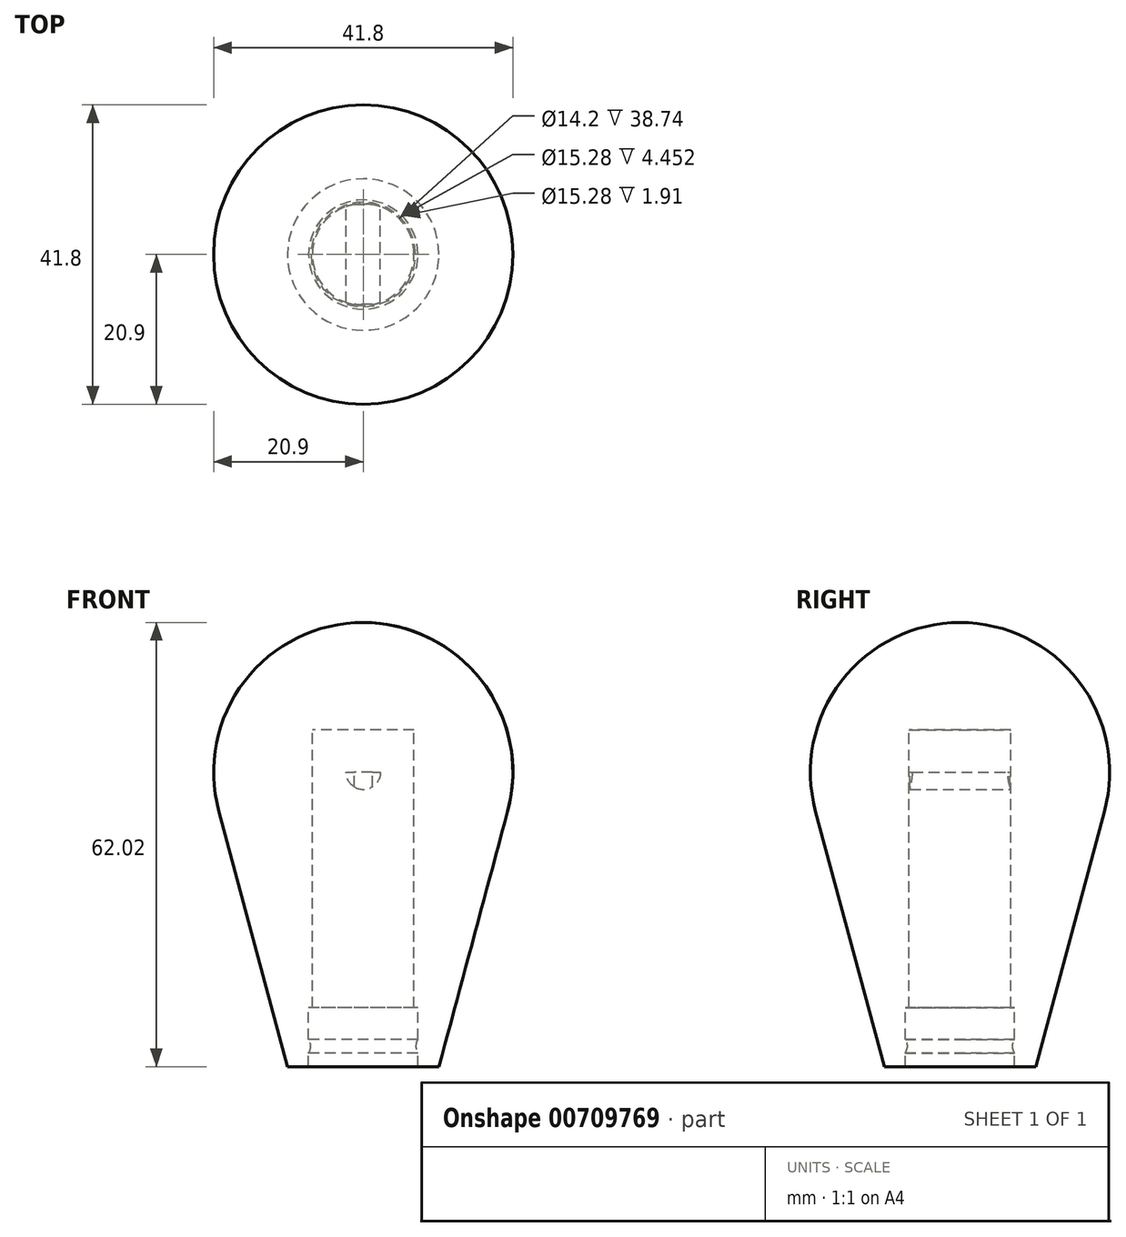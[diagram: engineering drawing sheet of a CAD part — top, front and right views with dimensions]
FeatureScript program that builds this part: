
annotation { "Feature Type Name" : "Feature", "Feature Type Description" : "" }
export const myFeature = defineFeature(function(context is Context, id is Id, definition is map)
    precondition{}
    {
        {
            var Q0;
            Q0=qCreatedBy(makeId("Front.planeOp"),FACE);
            var sketch = newSketch(context, id + "F0", { "sketchPlane" : qUnion([Q0])});
            skLineSegment(sketch, "E0", {"start": v(0, 0) * mm, "end": v(7.1, 0) * mm});
            skLineSegment(sketch, "E1", {"start": v(20.18, -11.3) * mm, "end": v(10.58, -47) * mm});
            skLineSegment(sketch, "E2", {"start": v(7.1, 0) * mm, "end": v(7.1, -38.74) * mm});
            skLineSegment(sketch, "E3", {"start": v(7.64, -47) * mm, "end": v(10.58, -47) * mm});
            skLineSegment(sketch, "E4", {"start": v(7.64, -38.74) * mm, "end": v(7.1, -38.74) * mm});
            skLineSegment(sketch, "E5", {"start": v(0, 0) * mm, "end": v(2.4, 0) * mm});
            skLineSegment(sketch, "E6", {"start": v(2.4, 0) * mm, "end": v(2.4, -5.88) * mm});
            skLineSegment(sketch, "E7", {"start": v(2.4, -5.88) * mm, "end": v(0, -5.88) * mm});
            skLineSegment(sketch, "E8", {"start": v(0, -5.88) * mm, "end": v(-2.4, -5.88) * mm});
            skLineSegment(sketch, "E9", {"start": v(-2.4, -5.88) * mm, "end": v(-2.4, 0) * mm});
            skLineSegment(sketch, "E10", {"start": v(-2.4, 0) * mm, "end": v(0, 0) * mm});
            skArc(sketch, "E11", {"start": v(2.4, -5.88) * mm, "mid": v(0, -8.28) * mm, "end": v(-2.4, -5.88) * mm});
            skLineSegment(sketch, "E12", {"start": v(7.64, -47) * mm, "end": v(7.64, -44.14) * mm});
            skLineSegment(sketch, "E13", {"start": v(7.64, -44.14) * mm, "end": v(7.64, -38.74) * mm});
            skLineSegment(sketch, "E14", {"start": v(7.64, -44.14) * mm, "end": v(7.34, -44.14) * mm});
            skLineSegment(sketch, "E15", {"start": v(7.64, -44.14) * mm, "end": v(7.64, -43.2) * mm});
            skLineSegment(sketch, "E16", {"start": v(7.64, -44.14) * mm, "end": v(7.64, -45.1) * mm});
            skArc(sketch, "E17", {"start": v(7.64, -43.2) * mm, "mid": v(7.34, -44.14) * mm, "end": v(7.64, -45.1) * mm});
            skArc(sketch, "E18", {"start": v(0, 15.02) * mm, "mid": v(16.58, 6.83) * mm, "end": v(20.18, -11.3) * mm});
            skLineSegment(sketch, "E19", {"start": v(0, 15.02) * mm, "end": v(0, 0) * mm});
            skSolve(sketch);
        }
        {
            var Q0;
            Q0=makeQuery(id+"F0.imprint","IMPRINT",FACE,{"disambiguationData":[TD([[makeQuery(id+"F0.imprint","IMPRINT",EDGE,{"derivedFrom":sQuery(id+"F0.wireOp",EDGE,"E5")}),-1.0]])]});
            var Q1;
            Q1=makeQuery(id+"F0.imprint","IMPRINT",FACE,{"disambiguationData":[TD([[makeQuery(id+"F0.imprint","IMPRINT",EDGE,{"derivedFrom":sQuery(id+"F0.wireOp",EDGE,"E7")}),1.0]])]});
            extrude(context, id + "F1", {"entities" : qUnion([Q0, Q1]), "endBound" : BoundingType.SYMMETRIC, "depth" : 13.97 * mm, "offsetDistance" : 25.4 * mm});
        }
        {
            var Q0;
            Q0=makeQuery(id+"F0.imprint","IMPRINT",FACE,{"disambiguationData":[TD([[makeQuery(id+"F0.imprint","IMPRINT",EDGE,{"derivedFrom":sQuery(id+"F0.wireOp",EDGE,"E0")}),1.0]])]});
            var Q1;
            {var subQ0=sQuery(id+"F0.wireOp",EDGE,"E14");Q1=makeQuery(id+"F0.imprint","IMPRINT",FACE,{"disambiguationData":[TD([[makeQuery(id+"F0.imprint","IMPRINT",EDGE,{"derivedFrom":subQ0}),-1.0]])]});}
            var Q2;
            {var subQ0=sQuery(id+"F0.wireOp",EDGE,"E14");Q2=makeQuery(id+"F0.imprint","IMPRINT",FACE,{"disambiguationData":[TD([[makeQuery(id+"F0.imprint","IMPRINT",EDGE,{"derivedFrom":subQ0}),1.0]])]});}
            var Q3;
            Q3=sQuery(id+"F0.wireOp",EDGE,"E19");
            revolve(context, id + "F2", {"operationType" : NewBodyOperationType.ADD, "entities" : qUnion([Q0, Q1, Q2]), "axis" : qUnion([Q3]), "revolveType" : RevolveType.FULL});
        }
    });
